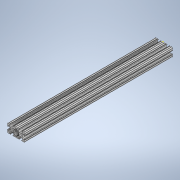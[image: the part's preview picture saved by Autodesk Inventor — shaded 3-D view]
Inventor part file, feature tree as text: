
AUTODESK INVENTOR PART (.ipt)
format: ipt  version: 2020 (Build 240168000, 168)  size: 335,872 bytes
history: native  units: in
note: dims shown in document units (in); Inventor stores cm internally (conversion verified against a paired STEP export)
features: sketch x2, extrude x1
ambient origin geometry x8: Origin, YZ Plane, XZ Plane, XY Plane, X Axis, Y Axis, Z Axis, Center Point
bodies: Solid1 (feature_tree)
feature tree (3):
  extrude  "Extrusion1"  [1 undecoded]
  sketch  "Sketch2"
  sketch  "Sketch1"  dims[d0=17.0in d1=0.0in]
note: 1 required parameter value undecoded (feature->parameter linkage not recoverable at this tier; creation-order binding heuristic only, values carry confidence <= 0.55)
